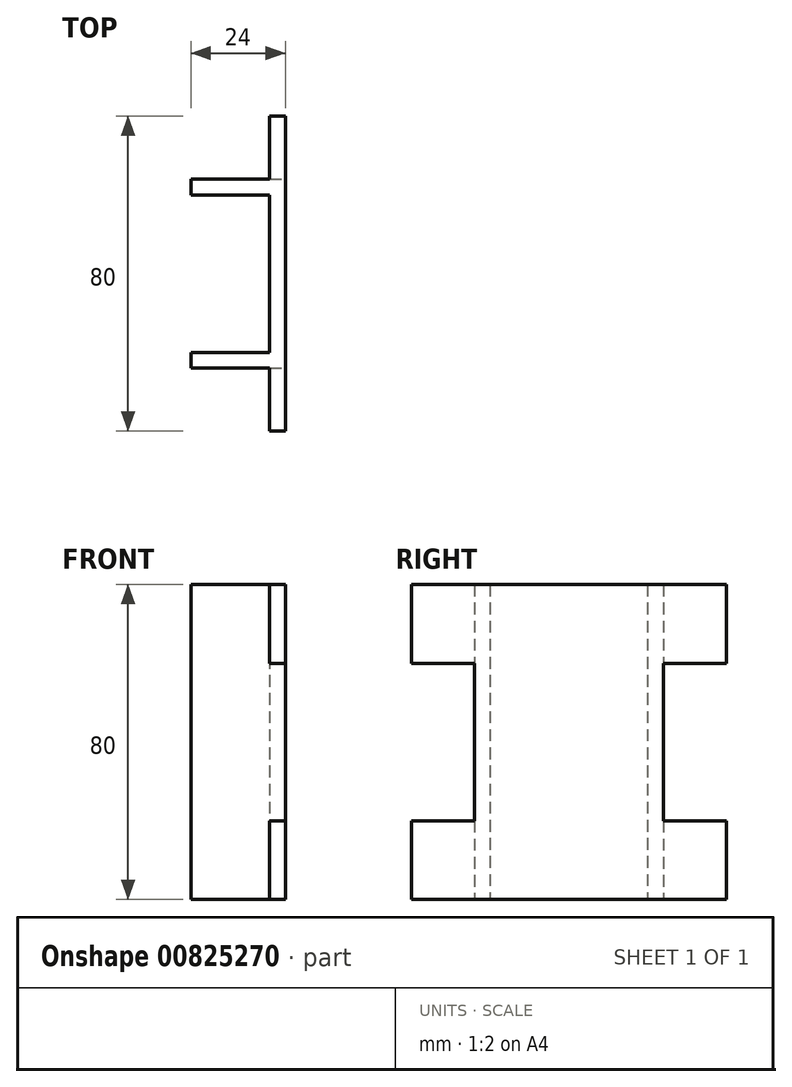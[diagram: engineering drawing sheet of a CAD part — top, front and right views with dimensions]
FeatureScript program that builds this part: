
annotation { "Feature Type Name" : "Feature", "Feature Type Description" : "" }
export const myFeature = defineFeature(function(context is Context, id is Id, definition is map)
    precondition{}
    {
        {
            var Q0;
            Q0=qCreatedBy(makeId("Top.planeOp"),FACE);
            var sketch = newSketch(context, id + "F0", { "sketchPlane" : qUnion([Q0])});
            skLineSegment(sketch, "E0", {"start": v(0, 0) * mm, "end": v(0, -4) * mm});
            skLineSegment(sketch, "E1", {"start": v(0, -4) * mm, "end": v(20, -4) * mm});
            skLineSegment(sketch, "E2", {"start": v(20, -4) * mm, "end": v(20, -44) * mm});
            skLineSegment(sketch, "E3", {"start": v(20, -44) * mm, "end": v(0, -44) * mm});
            skLineSegment(sketch, "E4", {"start": v(0, -44) * mm, "end": v(0, -48) * mm});
            skLineSegment(sketch, "E5", {"start": v(0, -48) * mm, "end": v(20, -48) * mm});
            skLineSegment(sketch, "E6", {"start": v(20, -48) * mm, "end": v(20, -64) * mm});
            skLineSegment(sketch, "E7", {"start": v(20, -64) * mm, "end": v(24, -64) * mm});
            skLineSegment(sketch, "E8", {"start": v(24, -64) * mm, "end": v(24, 16) * mm});
            skLineSegment(sketch, "E9", {"start": v(24, 16) * mm, "end": v(20, 16) * mm});
            skLineSegment(sketch, "E10", {"start": v(20, 16) * mm, "end": v(20, 0) * mm});
            skLineSegment(sketch, "E11", {"start": v(20, 0) * mm, "end": v(0, 0) * mm});
            skSolve(sketch);
        }
        {
            var Q0;
            Q0 = qSketchRegion(id + "F0", true);
            extrude(context, id + "F1", {"entities" : qUnion([Q0]), "depth" : 80 * mm, "offsetDistance" : 25 * mm});
        }
        {
            var Q0;
            Q0=makeQuery(id+"F1.opExtrude","SWEPT_FACE",FACE,{"disambiguationData":[OSD([sQuery(id+"F0.wireOp",EDGE,"E8")])]});
            var sketch = newSketch(context, id + "F2", { "sketchPlane" : qUnion([Q0])});
            skLineSegment(sketch, "E12.0.0", {"start": v(-48, 0) * mm, "end": v(-64, 0) * mm, "construction": true});
            skLineSegment(sketch, "E12.0.1", {"start": v(-64, 0) * mm, "end": v(-64, 80) * mm, "construction": true});
            skLineSegment(sketch, "E12.0.2", {"start": v(-64, 80) * mm, "end": v(-48, 80) * mm, "construction": true});
            skLineSegment(sketch, "E12.0.3", {"start": v(-48, 80) * mm, "end": v(-48, 0) * mm, "construction": true});
            skLineSegment(sketch, "E13.0.0", {"start": v(16, 0) * mm, "end": v(0, 0) * mm, "construction": true});
            skLineSegment(sketch, "E13.0.1", {"start": v(0, 0) * mm, "end": v(0, 80) * mm, "construction": true});
            skLineSegment(sketch, "E13.0.2", {"start": v(0, 80) * mm, "end": v(16, 80) * mm, "construction": true});
            skLineSegment(sketch, "E13.0.3", {"start": v(16, 80) * mm, "end": v(16, 0) * mm, "construction": true});
            skLineSegment(sketch, "E14.0.0", {"start": v(-4, 0) * mm, "end": v(-44, 0) * mm, "construction": true});
            skLineSegment(sketch, "E14.0.1", {"start": v(-44, 0) * mm, "end": v(-44, 80) * mm, "construction": true});
            skLineSegment(sketch, "E14.0.2", {"start": v(-44, 80) * mm, "end": v(-4, 80) * mm, "construction": true});
            skLineSegment(sketch, "E14.0.3", {"start": v(-4, 80) * mm, "end": v(-4, 0) * mm, "construction": true});
            skLineSegment(sketch, "E15.bottom", {"start": v(16, 60) * mm, "end": v(0, 60) * mm});
            skLineSegment(sketch, "E15.top", {"start": v(16, 20) * mm, "end": v(0, 20) * mm});
            skLineSegment(sketch, "E15.left", {"start": v(16, 60) * mm, "end": v(16, 20) * mm});
            skLineSegment(sketch, "E15.right", {"start": v(0, 60) * mm, "end": v(0, 20) * mm});
            skLineSegment(sketch, "E16.bottom", {"start": v(-48, 60) * mm, "end": v(-64, 60) * mm});
            skLineSegment(sketch, "E16.top", {"start": v(-48, 20) * mm, "end": v(-64, 20) * mm});
            skLineSegment(sketch, "E16.left", {"start": v(-48, 60) * mm, "end": v(-48, 20) * mm});
            skLineSegment(sketch, "E16.right", {"start": v(-64, 60) * mm, "end": v(-64, 20) * mm});
            skSolve(sketch);
        }
        {
            var Q0;
            Q0 = qSketchRegion(id + "F2", true);
            extrude(context, id + "F3", {"entities" : qUnion([Q0]), "operationType" : NewBodyOperationType.REMOVE, "endBound" : BoundingType.THROUGH_ALL, "oppositeDirection" : true, "depth" : 25 * mm, "offsetDistance" : 25 * mm});
        }
    });
